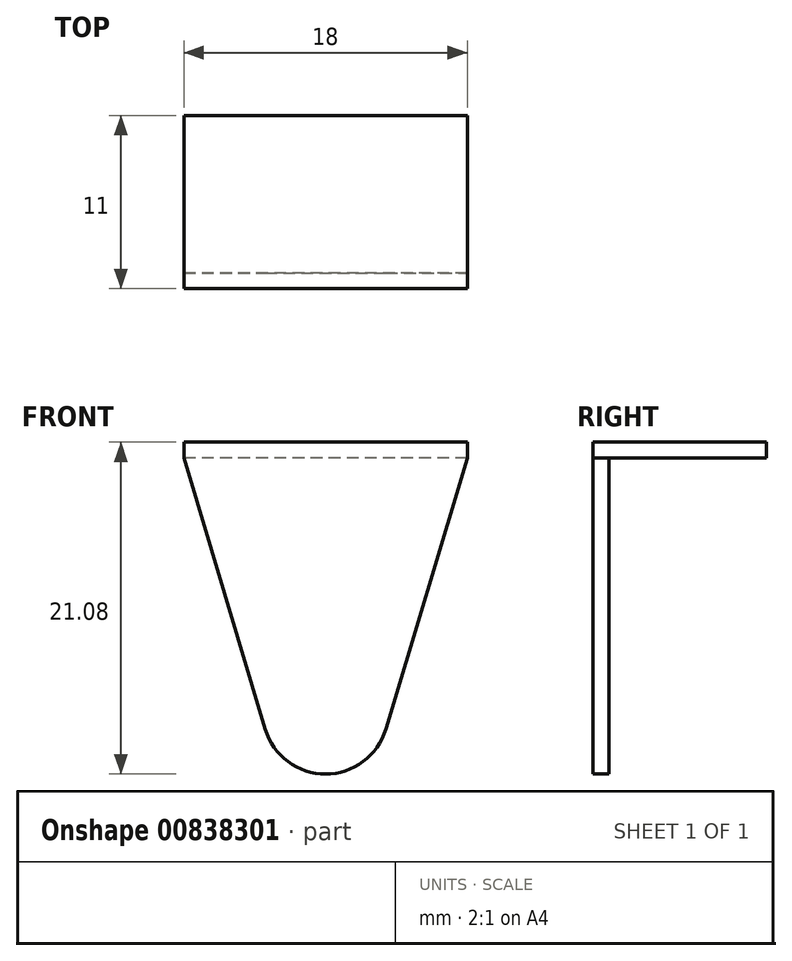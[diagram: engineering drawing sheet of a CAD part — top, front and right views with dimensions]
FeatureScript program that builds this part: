
annotation { "Feature Type Name" : "Feature", "Feature Type Description" : "" }
export const myFeature = defineFeature(function(context is Context, id is Id, definition is map)
    precondition{}
    {
        {
            var Q0;
            Q0=qCreatedBy(makeId("Front.planeOp"),FACE);
            var sketch = newSketch(context, id + "F0", { "sketchPlane" : qUnion([Q0])});
            skLineSegment(sketch, "E0.bottom", {"start": v(-9, 30) * mm, "end": v(9, 30) * mm});
            skLineSegment(sketch, "E0.top", {"start": v(-9, -30) * mm, "end": v(9, -30) * mm});
            skLineSegment(sketch, "E0.left", {"start": v(-9, 30) * mm, "end": v(-9, -30) * mm});
            skLineSegment(sketch, "E0.right", {"start": v(9, 30) * mm, "end": v(9, -30) * mm});
            skLineSegment(sketch, "E1", {"start": v(0, 30) * mm, "end": v(0, 0) * mm, "construction": true});
            skCircle(sketch, "E2", {"center": v(0, 19.5) * mm, "radius": 5.5 * mm});
            skSolve(sketch);
        }
        {
            var Q0;
            Q0=qCreatedBy(makeId("Front.planeOp"),FACE);
            var sketch = newSketch(context, id + "F1", { "sketchPlane" : qUnion([Q0])});
            skLineSegment(sketch, "E3", {"start": v(-9, 30) * mm, "end": v(0, 0) * mm});
            skLineSegment(sketch, "E4", {"start": v(0, 0) * mm, "end": v(9, 30) * mm});
            skLineSegment(sketch, "E5", {"start": v(9, 30) * mm, "end": v(-9, 30) * mm});
            skSolve(sketch);
        }
        {
            var Q0;
            Q0 = qSketchRegion(id + "F1", true);
            extrude(context, id + "F2", {"entities" : qUnion([Q0]), "depth" : 1 * mm, "offsetDistance" : 25.4 * mm});
        }
        {
            var Q0;
            Q0=makeQuery(id+"F2.opExtrude","SWEPT_EDGE",EDGE,{"disambiguationData":[OSD([sQuery(id+"F1.wireOp",EDGE,"E3"),sQuery(id+"F1.wireOp",EDGE,"E4")])]});
            fillet(context, id + "F3", {"entities" : qUnion([Q0]), "radius" : 4 * mm, "tangentPropagation" : true, "allowEdgeOverflow" : false});
        }
        {
            var Q0;
            Q0=makeQuery(id+"F0.imprint","IMPRINT",FACE,{"disambiguationData":[TD([[makeQuery(id+"F0.imprint","IMPRINT",EDGE,{"derivedFrom":sQuery(id+"F0.wireOp",EDGE,"E0.bottom")}),-1.0]])]});
            var sketch = newSketch(context, id + "F4", { "sketchPlane" : qUnion([Q0])});
            skLineSegment(sketch, "E6.bottom", {"start": v(-9, 30) * mm, "end": v(9, 30) * mm});
            skLineSegment(sketch, "E6.top", {"start": v(-9, 31) * mm, "end": v(9, 31) * mm});
            skLineSegment(sketch, "E6.left", {"start": v(-9, 30) * mm, "end": v(-9, 31) * mm});
            skLineSegment(sketch, "E6.right", {"start": v(9, 30) * mm, "end": v(9, 31) * mm});
            skSolve(sketch);
        }
        {
            var Q0;
            Q0 = qSketchRegion(id + "F4", true);
            extrude(context, id + "F5", {"entities" : qUnion([Q0]), "operationType" : NewBodyOperationType.ADD, "depth" : 1 * mm, "offsetDistance" : 25.4 * mm, "hasSecondDirection" : true, "secondDirectionOppositeDirection" : true, "secondDirectionDepth" : 10 * mm});
        }
    });
